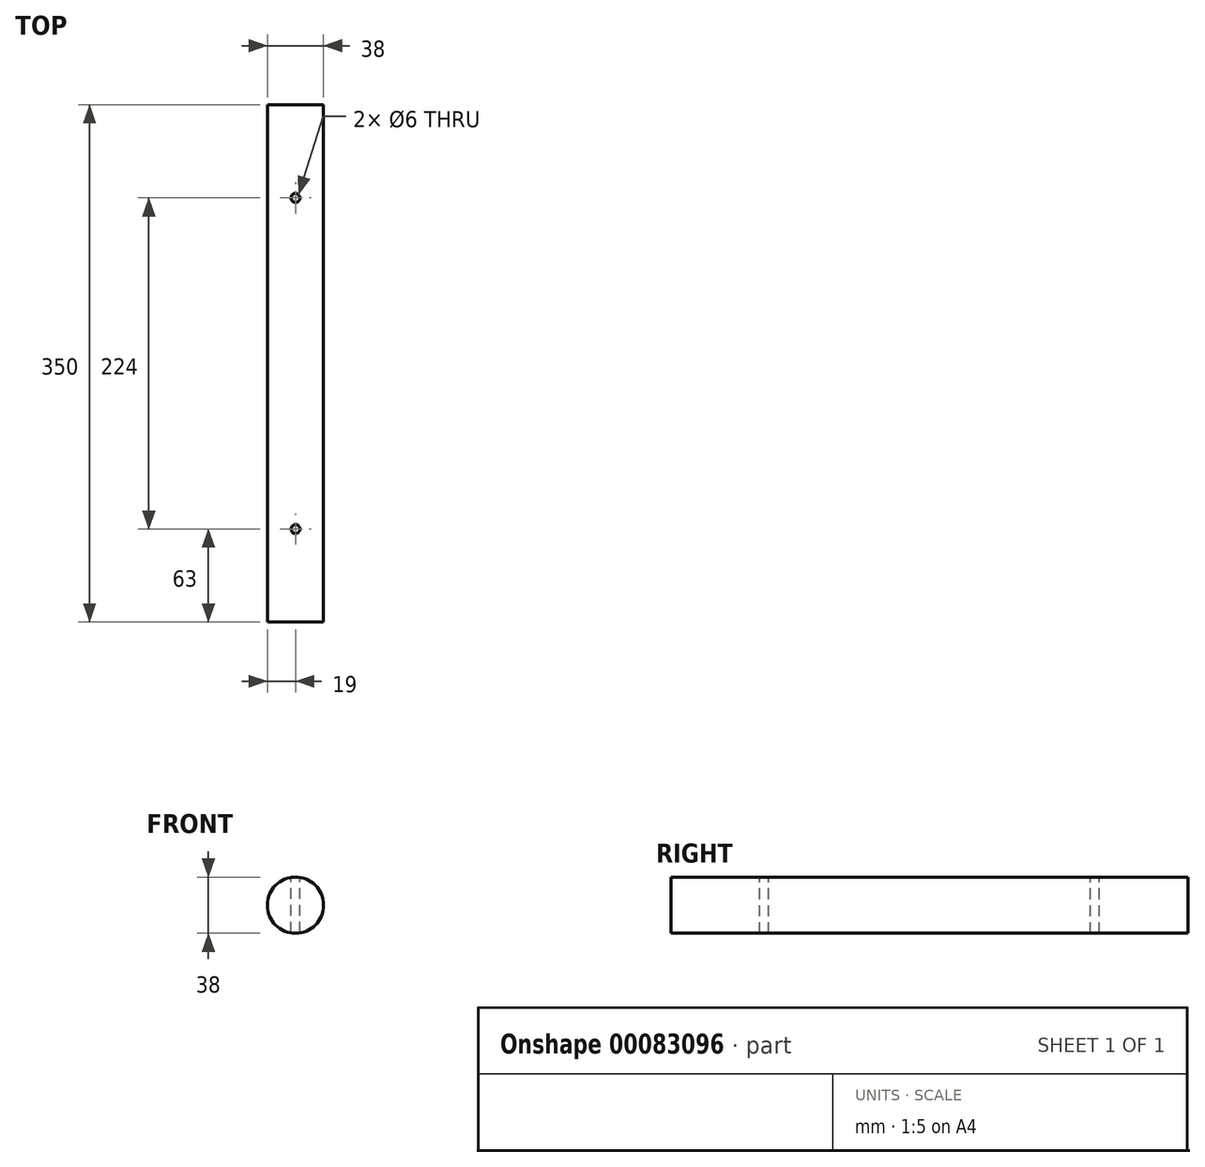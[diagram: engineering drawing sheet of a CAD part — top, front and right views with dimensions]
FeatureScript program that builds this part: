
annotation { "Feature Type Name" : "Feature", "Feature Type Description" : "" }
export const myFeature = defineFeature(function(context is Context, id is Id, definition is map)
    precondition{}
    {
        {
            var Q0;
            Q0=qCreatedBy(makeId("Front.planeOp"),FACE);
            var sketch = newSketch(context, id + "F0", { "sketchPlane" : qUnion([Q0])});
            skCircle(sketch, "E0", {"center": v(0, 0) * mm, "radius": 19 * mm});
            skSolve(sketch);
        }
        {
            var Q0;
            Q0 = qSketchRegion(id + "F0", true);
            extrude(context, id + "F1", {"entities" : qUnion([Q0]), "depth" : 350 * mm});
        }
        {
            var Q0;
            Q0=qCreatedBy(makeId("Top.planeOp"),FACE);
            cPlane(context, id + "F2", {"entities" : qUnion([Q0]), "cplaneType" : CPlaneType.OFFSET, "offset" : (38 / 2) * mm, "width" : 150 * mm, "height" : 150 * mm});
        }
        {
            var Q0;
            Q0=qCreatedBy(id+"F2.planeOp",FACE);
            var sketch = newSketch(context, id + "F3", { "sketchPlane" : qUnion([Q0])});
            skCircle(sketch, "E1", {"center": v(0, -63) * mm, "radius": 3 * mm});
            skCircle(sketch, "E2", {"center": v(0, -287) * mm, "radius": 3 * mm});
            skSolve(sketch);
        }
        {
            var Q0;
            Q0 = qSketchRegion(id + "F3", true);
            extrude(context, id + "F4", {"entities" : qUnion([Q0]), "operationType" : NewBodyOperationType.REMOVE, "endBound" : BoundingType.THROUGH_ALL, "oppositeDirection" : true, "depth" : 25 * mm});
        }
    });
